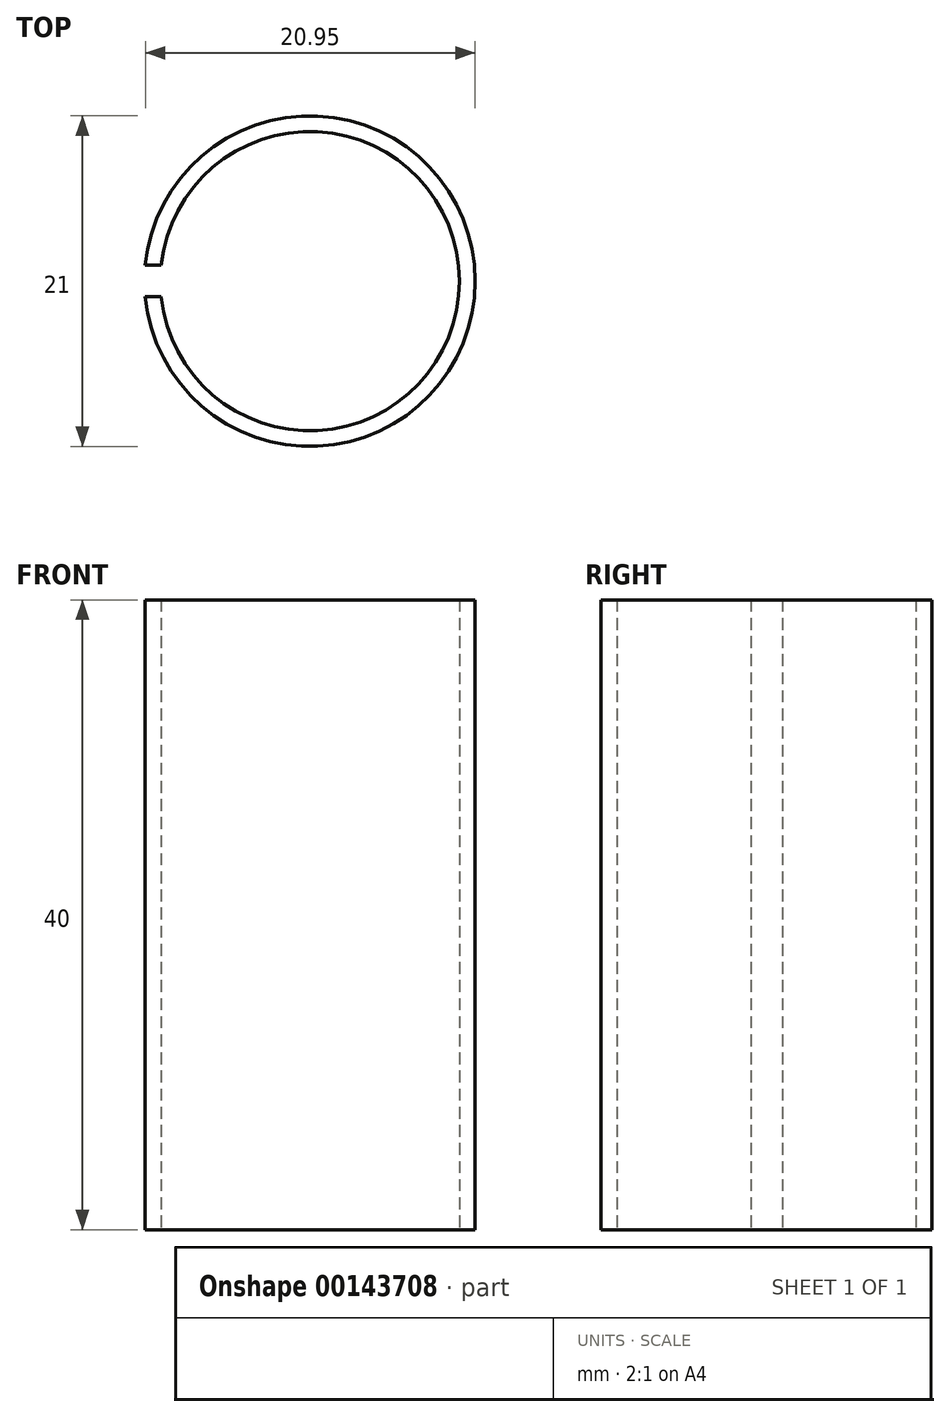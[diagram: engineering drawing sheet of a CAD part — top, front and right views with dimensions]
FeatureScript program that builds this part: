
annotation { "Feature Type Name" : "Feature", "Feature Type Description" : "" }
export const myFeature = defineFeature(function(context is Context, id is Id, definition is map)
    precondition{}
    {
        {
            var Q0;
            Q0=qCreatedBy(makeId("Top.planeOp"),FACE);
            var sketch = newSketch(context, id + "F0", { "sketchPlane" : qUnion([Q0])});
            skCircle(sketch, "E0", {"center": v(-88.5, -95) * mm, "radius": 9.5 * mm});
            skCircle(sketch, "E1.0", {"center": v(-88.5, -95) * mm, "radius": 10.5 * mm});
            skSolve(sketch);
        }
        {
            var Q0;
            Q0 = qSketchRegion(id + "F0", true);
            extrude(context, id + "F1", {"entities" : qUnion([Q0]), "depth" : 40 * mm});
        }
        {
            var Q0;
            Q0=makeQuery(id+"F1.opExtrude","CAP_FACE",FACE,{"disambiguationData":[OSD([sQuery(id+"F0.wireOp",EDGE,"E0"),sQuery(id+"F0.wireOp",EDGE,"E1.0")])],"isStart":false});
            var sketch = newSketch(context, id + "F2", { "sketchPlane" : qUnion([Q0])});
            skLineSegment(sketch, "E2.bottom", {"start": v(-102.63, -94) * mm, "end": v(-97.63, -94) * mm});
            skLineSegment(sketch, "E2.top", {"start": v(-102.63, -96) * mm, "end": v(-97.63, -96) * mm});
            skLineSegment(sketch, "E2.left", {"start": v(-102.63, -94) * mm, "end": v(-102.63, -96) * mm});
            skLineSegment(sketch, "E2.right", {"start": v(-97.63, -94) * mm, "end": v(-97.63, -96) * mm});
            skPoint(sketch, "E3", {"position": v(-88.5, -95) * mm});
            skSolve(sketch);
        }
        {
            var Q0;
            Q0 = qSketchRegion(id + "F2", true);
            extrude(context, id + "F3", {"entities" : qUnion([Q0]), "operationType" : NewBodyOperationType.REMOVE, "endBound" : BoundingType.THROUGH_ALL, "oppositeDirection" : true, "depth" : 25 * mm});
        }
        {
            var Q0;
            Q0=makeQuery(id+"F1.opExtrude","SWEPT_BODY",BODY,{"disambiguationData":[OSD([sQuery(id+"F0.wireOp",EDGE,"E0"),sQuery(id+"F0.wireOp",EDGE,"E1.0")])]});
            transform(context, id + "F4", {"entities" : qUnion([Q0]), "transformType" : TransformType.TRANSLATION_3D, "dx" : 0 * mm, "dy" : 0 * mm, "dz" : 50 * mm, "makeCopy" : false});
        }
    });
